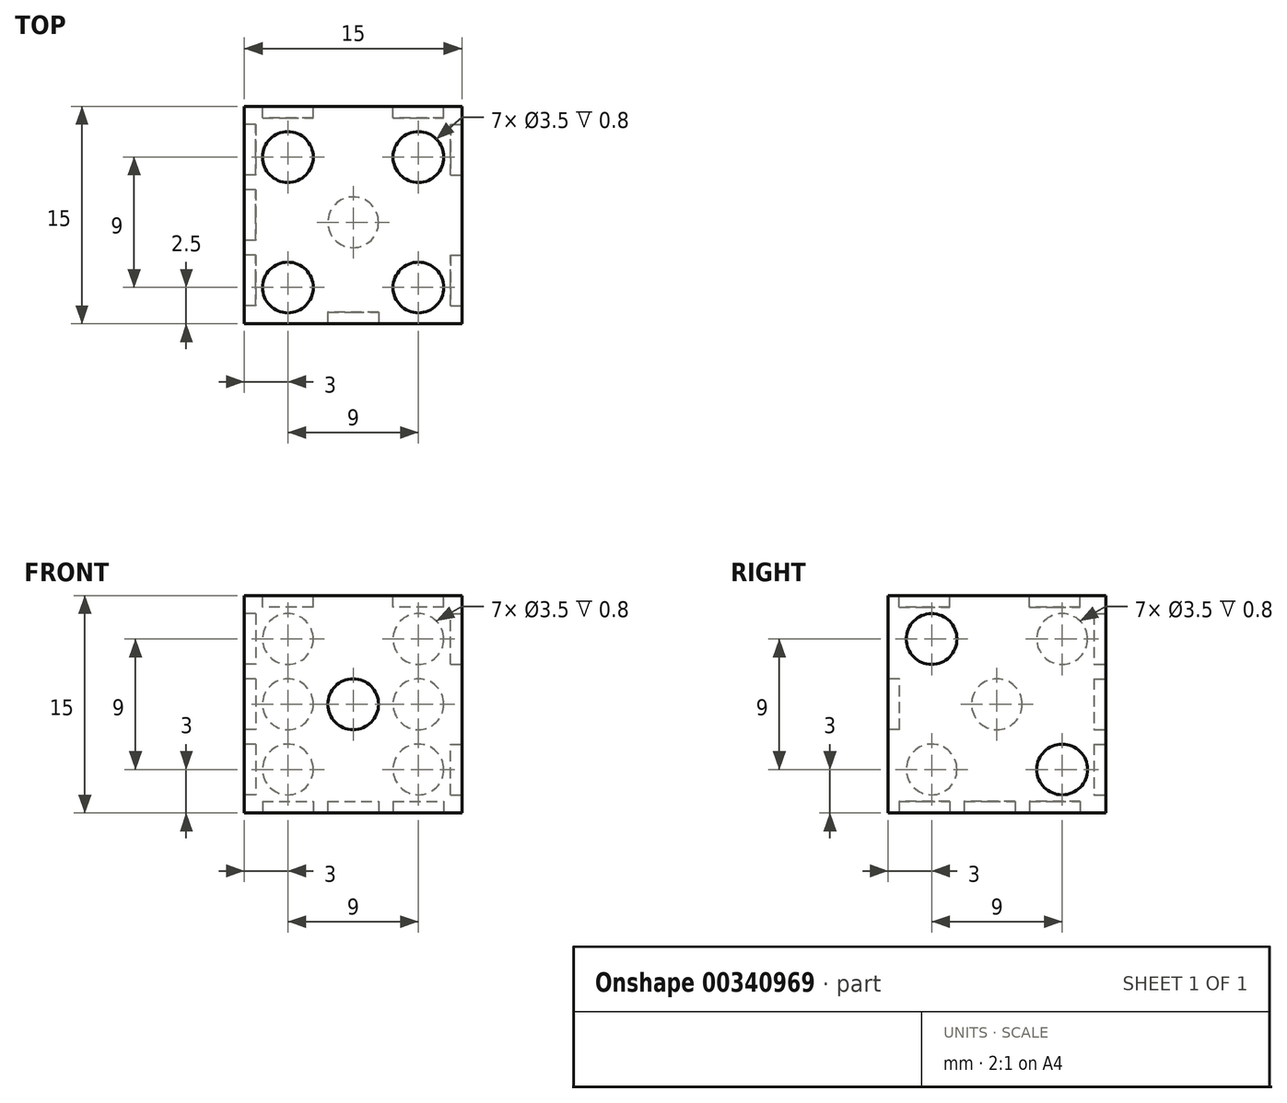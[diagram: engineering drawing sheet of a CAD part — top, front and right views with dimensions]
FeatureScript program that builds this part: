
annotation { "Feature Type Name" : "Feature", "Feature Type Description" : "" }
export const myFeature = defineFeature(function(context is Context, id is Id, definition is map)
    precondition{}
    {
        {
            var Q0;
            Q0=qCreatedBy(makeId("Front.planeOp"),FACE);
            var sketch = newSketch(context, id + "F0", { "sketchPlane" : qUnion([Q0])});
            skLineSegment(sketch, "E0.bottom", {"start": v(0, 0) * mm, "end": v(15, 0) * mm});
            skLineSegment(sketch, "E0.top", {"start": v(0, 15) * mm, "end": v(15, 15) * mm});
            skLineSegment(sketch, "E0.left", {"start": v(0, 0) * mm, "end": v(0, 15) * mm});
            skLineSegment(sketch, "E0.right", {"start": v(15, 0) * mm, "end": v(15, 15) * mm});
            skSolve(sketch);
        }
        {
            var Q0;
            Q0 = qSketchRegion(id + "F0", true);
            extrude(context, id + "F1", {"entities" : qUnion([Q0]), "depth" : 15 * mm});
        }
        {
            var Q0;
            Q0=makeQuery(id+"F1.opExtrude","CAP_FACE",FACE,{"disambiguationData":[OSD([sQuery(id+"F0.wireOp",EDGE,"E0.bottom"),sQuery(id+"F0.wireOp",EDGE,"E0.top"),sQuery(id+"F0.wireOp",EDGE,"E0.left"),sQuery(id+"F0.wireOp",EDGE,"E0.right")])],"isStart":false});
            var sketch = newSketch(context, id + "F2", { "sketchPlane" : qUnion([Q0])});
            skCircle(sketch, "E1", {"center": v(7.5, 7.5) * mm, "radius": 1.75 * mm});
            skPoint(sketch, "E1.centerSnap0", {"position": v(15, 7.5) * mm});
            skPoint(sketch, "E1.centerSnap1", {"position": v(7.5, 15) * mm});
            skSolve(sketch);
        }
        {
            var Q0;
            Q0=makeQuery(id+"F1.opExtrude","CAP_FACE",FACE,{"disambiguationData":[OSD([sQuery(id+"F0.wireOp",EDGE,"E0.bottom"),sQuery(id+"F0.wireOp",EDGE,"E0.top"),sQuery(id+"F0.wireOp",EDGE,"E0.left"),sQuery(id+"F0.wireOp",EDGE,"E0.right")])],"isStart":true});
            var sketch = newSketch(context, id + "F3", { "sketchPlane" : qUnion([Q0])});
            skCircle(sketch, "E2", {"center": v(-12, 12) * mm, "radius": 1.75 * mm});
            skCircle(sketch, "E3.0.1.0", {"center": v(-12, 7.5) * mm, "radius": 1.75 * mm});
            skCircle(sketch, "E3.0.2.0", {"center": v(-12, 3) * mm, "radius": 1.75 * mm});
            skCircle(sketch, "E3.1.0.0", {"center": v(-3, 12) * mm, "radius": 1.75 * mm});
            skCircle(sketch, "E3.1.1.0", {"center": v(-3, 7.5) * mm, "radius": 1.75 * mm});
            skCircle(sketch, "E3.1.2.0", {"center": v(-3, 3) * mm, "radius": 1.75 * mm});
            skLineSegment(sketch, "E3.direction1", {"start": v(-12, 12) * mm, "end": v(-3, 12) * mm, "construction": true});
            skLineSegment(sketch, "E3.direction2", {"start": v(-12, 12) * mm, "end": v(-12, 7.5) * mm, "construction": true});
            skSolve(sketch);
        }
        {
            var Q0;
            Q0 = qSketchRegion(id + "F2", true);
            extrude(context, id + "F4", {"entities" : qUnion([Q0]), "oppositeDirection" : true, "depth" : 0.8 * mm});
        }
        {
            var Q0;
            Q0 = qSketchRegion(id + "F3", true);
            extrude(context, id + "F5", {"entities" : qUnion([Q0]), "oppositeDirection" : true, "depth" : 0.8 * mm});
        }
        {
            var Q0;
            Q0=makeQuery(id+"F1.opExtrude","SWEPT_FACE",FACE,{"disambiguationData":[OSD([sQuery(id+"F0.wireOp",EDGE,"E0.right")])]});
            var sketch = newSketch(context, id + "F6", { "sketchPlane" : qUnion([Q0])});
            skCircle(sketch, "E4", {"center": v(-12, 12) * mm, "radius": 1.75 * mm});
            skCircle(sketch, "E5", {"center": v(-3, 3) * mm, "radius": 1.75 * mm});
            skSolve(sketch);
        }
        {
            var Q0;
            Q0 = qSketchRegion(id + "F6", true);
            extrude(context, id + "F7", {"entities" : qUnion([Q0]), "oppositeDirection" : true, "depth" : 0.8 * mm});
        }
        {
            var Q0;
            Q0=makeQuery(id+"F1.opExtrude","SWEPT_FACE",FACE,{"disambiguationData":[OSD([sQuery(id+"F0.wireOp",EDGE,"E0.left")])]});
            var sketch = newSketch(context, id + "F8", { "sketchPlane" : qUnion([Q0])});
            skCircle(sketch, "E6", {"center": v(3, 12) * mm, "radius": 1.75 * mm});
            skCircle(sketch, "E7.0.2.0", {"center": v(3, 3) * mm, "radius": 1.75 * mm});
            skCircle(sketch, "E7.1.0.0", {"center": v(12, 12) * mm, "radius": 1.75 * mm});
            skCircle(sketch, "E7.1.2.0", {"center": v(12, 3) * mm, "radius": 1.75 * mm});
            skLineSegment(sketch, "E7.direction1", {"start": v(3, 12) * mm, "end": v(12, 12) * mm, "construction": true});
            skLineSegment(sketch, "E7.direction2", {"start": v(3, 12) * mm, "end": v(3, 7.5) * mm, "construction": true});
            skCircle(sketch, "E8", {"center": v(7.5, 7.5) * mm, "radius": 1.75 * mm});
            skPoint(sketch, "E8.centerSnap0", {"position": v(15, 7.5) * mm});
            skPoint(sketch, "E8.centerSnap1", {"position": v(7.5, 15) * mm});
            skSolve(sketch);
        }
        {
            var Q0;
            Q0 = qSketchRegion(id + "F8", true);
            extrude(context, id + "F9", {"entities" : qUnion([Q0]), "oppositeDirection" : true, "depth" : 0.8 * mm});
        }
        {
            var Q0;
            Q0=makeQuery(id+"F1.opExtrude","SWEPT_FACE",FACE,{"disambiguationData":[OSD([sQuery(id+"F0.wireOp",EDGE,"E0.bottom")])]});
            var sketch = newSketch(context, id + "F10", { "sketchPlane" : qUnion([Q0])});
            skCircle(sketch, "E9.0.2.0", {"center": v(3, 3.5) * mm, "radius": 1.75 * mm});
            skCircle(sketch, "E9.1.0.0", {"center": v(12, 12.5) * mm, "radius": 1.75 * mm});
            skLineSegment(sketch, "E9.direction1", {"start": v(3, 12.5) * mm, "end": v(12, 12.5) * mm, "construction": true});
            skLineSegment(sketch, "E9.direction2", {"start": v(3, 12.5) * mm, "end": v(3, 8) * mm, "construction": true});
            skCircle(sketch, "E10", {"center": v(7.5, 8) * mm, "radius": 1.75 * mm});
            skPoint(sketch, "E10.centerSnap0", {"position": v(15, 8) * mm});
            skPoint(sketch, "E10.centerSnap1", {"position": v(7.5, 15.5) * mm});
            skPoint(sketch, "E11", {"position": v(7.5, 15) * mm});
            skSolve(sketch);
        }
        {
            var Q0;
            Q0 = qSketchRegion(id + "F10", true);
            extrude(context, id + "F11", {"entities" : qUnion([Q0]), "oppositeDirection" : true, "depth" : 0.8 * mm});
        }
        {
            var Q0;
            Q0=makeQuery(id+"F1.opExtrude","SWEPT_FACE",FACE,{"disambiguationData":[OSD([sQuery(id+"F0.wireOp",EDGE,"E0.top")])]});
            var sketch = newSketch(context, id + "F12", { "sketchPlane" : qUnion([Q0])});
            skCircle(sketch, "E12", {"center": v(3, -3.5) * mm, "radius": 1.75 * mm});
            skCircle(sketch, "E13.0.2.0", {"center": v(3, -12.5) * mm, "radius": 1.75 * mm});
            skCircle(sketch, "E13.1.0.0", {"center": v(12, -3.5) * mm, "radius": 1.75 * mm});
            skCircle(sketch, "E13.1.2.0", {"center": v(12, -12.5) * mm, "radius": 1.75 * mm});
            skLineSegment(sketch, "E13.direction1", {"start": v(3, -3.5) * mm, "end": v(12, -3.5) * mm, "construction": true});
            skLineSegment(sketch, "E13.direction2", {"start": v(3, -3.5) * mm, "end": v(3, -8) * mm, "construction": true});
            skPoint(sketch, "E14.centerSnap0", {"position": v(16.98, -11.79) * mm});
            skPoint(sketch, "E14.centerSnap1", {"position": v(9.48, -4.29) * mm});
            skSolve(sketch);
        }
        {
            var Q0;
            Q0 = qSketchRegion(id + "F12", true);
            extrude(context, id + "F13", {"entities" : qUnion([Q0]), "oppositeDirection" : true, "depth" : 0.8 * mm});
        }
        {
            var Q0;
            Q0=makeQuery(id+"F4.opExtrude","SWEPT_BODY",BODY,{"disambiguationData":[OSD([sQuery(id+"F2.wireOp",EDGE,"E1")])]});
            var Q1;
            Q1=makeQuery(id+"F5.opExtrude","SWEPT_BODY",BODY,{"disambiguationData":[OSD([sQuery(id+"F3.wireOp",EDGE,"E2")])]});
            var Q2;
            Q2=makeQuery(id+"F5.opExtrude","SWEPT_BODY",BODY,{"disambiguationData":[OSD([sQuery(id+"F3.wireOp",EDGE,"E3.0.1.0")])]});
            var Q3;
            Q3=makeQuery(id+"F5.opExtrude","SWEPT_BODY",BODY,{"disambiguationData":[OSD([sQuery(id+"F3.wireOp",EDGE,"E3.0.2.0")])]});
            var Q4;
            Q4=makeQuery(id+"F5.opExtrude","SWEPT_BODY",BODY,{"disambiguationData":[OSD([sQuery(id+"F3.wireOp",EDGE,"E3.1.0.0")])]});
            var Q5;
            Q5=makeQuery(id+"F5.opExtrude","SWEPT_BODY",BODY,{"disambiguationData":[OSD([sQuery(id+"F3.wireOp",EDGE,"E3.1.1.0")])]});
            var Q6;
            Q6=makeQuery(id+"F5.opExtrude","SWEPT_BODY",BODY,{"disambiguationData":[OSD([sQuery(id+"F3.wireOp",EDGE,"E3.1.2.0")])]});
            var Q7;
            Q7=makeQuery(id+"F7.opExtrude","SWEPT_BODY",BODY,{"disambiguationData":[OSD([sQuery(id+"F6.wireOp",EDGE,"E4")])]});
            var Q8;
            Q8=makeQuery(id+"F7.opExtrude","SWEPT_BODY",BODY,{"disambiguationData":[OSD([sQuery(id+"F6.wireOp",EDGE,"E5")])]});
            var Q9;
            Q9=makeQuery(id+"F9.opExtrude","SWEPT_BODY",BODY,{"disambiguationData":[OSD([sQuery(id+"F8.wireOp",EDGE,"E6")])]});
            var Q10;
            Q10=makeQuery(id+"F9.opExtrude","SWEPT_BODY",BODY,{"disambiguationData":[OSD([sQuery(id+"F8.wireOp",EDGE,"E7.0.2.0")])]});
            var Q11;
            Q11=makeQuery(id+"F9.opExtrude","SWEPT_BODY",BODY,{"disambiguationData":[OSD([sQuery(id+"F8.wireOp",EDGE,"E7.1.0.0")])]});
            var Q12;
            Q12=makeQuery(id+"F9.opExtrude","SWEPT_BODY",BODY,{"disambiguationData":[OSD([sQuery(id+"F8.wireOp",EDGE,"E7.1.2.0")])]});
            var Q13;
            Q13=makeQuery(id+"F9.opExtrude","SWEPT_BODY",BODY,{"disambiguationData":[OSD([sQuery(id+"F8.wireOp",EDGE,"E8")])]});
            var Q14;
            Q14=makeQuery(id+"F11.opExtrude","SWEPT_BODY",BODY,{"disambiguationData":[OSD([sQuery(id+"F10.wireOp",EDGE,"E9.0.2.0")])]});
            var Q15;
            Q15=makeQuery(id+"F11.opExtrude","SWEPT_BODY",BODY,{"disambiguationData":[OSD([sQuery(id+"F10.wireOp",EDGE,"E9.1.0.0")])]});
            var Q16;
            Q16=makeQuery(id+"F11.opExtrude","SWEPT_BODY",BODY,{"disambiguationData":[OSD([sQuery(id+"F10.wireOp",EDGE,"E10")])]});
            var Q17;
            Q17=makeQuery(id+"F13.opExtrude","SWEPT_BODY",BODY,{"disambiguationData":[OSD([sQuery(id+"F12.wireOp",EDGE,"E12")])]});
            var Q18;
            Q18=makeQuery(id+"F13.opExtrude","SWEPT_BODY",BODY,{"disambiguationData":[OSD([sQuery(id+"F12.wireOp",EDGE,"E13.0.2.0")])]});
            var Q19;
            Q19=makeQuery(id+"F13.opExtrude","SWEPT_BODY",BODY,{"disambiguationData":[OSD([sQuery(id+"F12.wireOp",EDGE,"E13.1.0.0")])]});
            var Q20;
            Q20=makeQuery(id+"F13.opExtrude","SWEPT_BODY",BODY,{"disambiguationData":[OSD([sQuery(id+"F12.wireOp",EDGE,"E13.1.2.0")])]});
            var Q21;
            Q21=makeQuery(id+"F1.opExtrude","SWEPT_BODY",BODY,{"disambiguationData":[OSD([sQuery(id+"F0.wireOp",EDGE,"E0.bottom"),sQuery(id+"F0.wireOp",EDGE,"E0.top"),sQuery(id+"F0.wireOp",EDGE,"E0.left"),sQuery(id+"F0.wireOp",EDGE,"E0.right")])]});
            booleanBodies(context, id + "F14", {"operationType" : BooleanOperationType.SUBTRACTION, "tools" : qUnion([Q0, Q1, Q2, Q3, Q4, Q5, Q6, Q7, Q8, Q9, Q10, Q11, Q12, Q13, Q14, Q15, Q16, Q17, Q18, Q19, Q20]), "targets" : qUnion([Q21]), "keepTools" : true});
        }
    });
